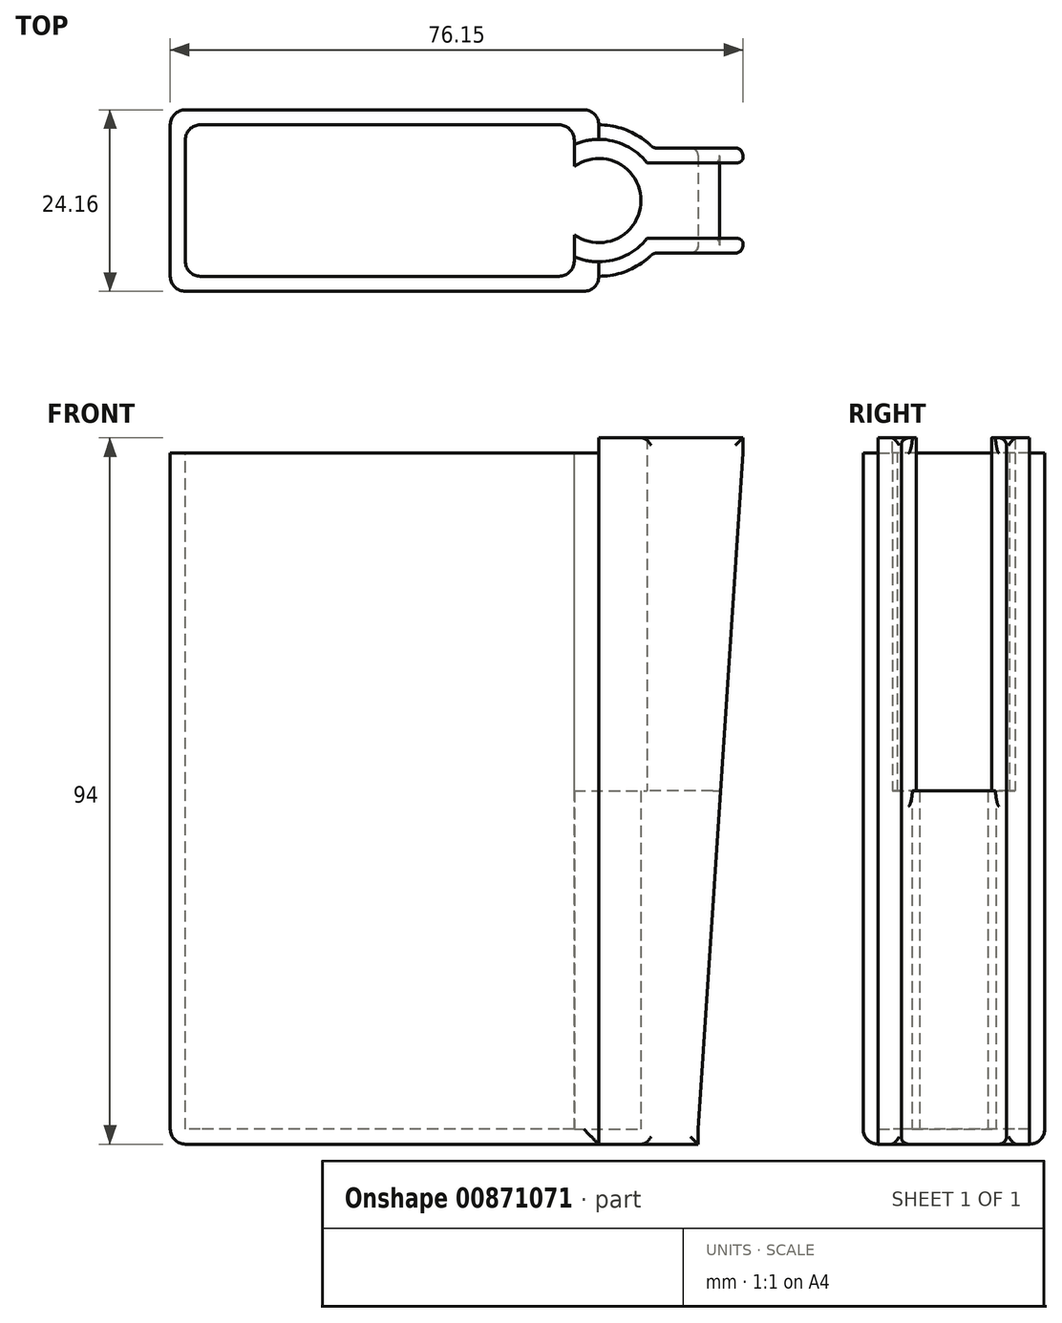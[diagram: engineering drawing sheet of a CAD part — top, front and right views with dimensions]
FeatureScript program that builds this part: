
annotation { "Feature Type Name" : "Feature", "Feature Type Description" : "" }
export const myFeature = defineFeature(function(context is Context, id is Id, definition is map)
    precondition{}
    {
        {
            var Q0;
            Q0=qCreatedBy(makeId("Top.planeOp"),FACE);
            var sketch = newSketch(context, id + "F0", { "sketchPlane" : qUnion([Q0])});
            skArc(sketch, "E0", {"start": v(6.44, 5) * mm, "mid": v(-8.15, 0) * mm, "end": v(6.44, -5) * mm});
            skLineSegment(sketch, "E1.bottom", {"start": v(19.15, 5) * mm, "end": v(8.66, 5) * mm});
            skLineSegment(sketch, "E1.top", {"start": v(19.15, -5) * mm, "end": v(8.66, -5) * mm});
            skLineSegment(sketch, "E2", {"start": v(-8.15, 0) * mm, "end": v(8.15, 0) * mm, "construction": true});
            skPoint(sketch, "E1.right.start.orphan", {"position": v(-27, 5) * mm});
            skPoint(sketch, "E3.orphan", {"position": v(-27, -5) * mm});
            skPoint(sketch, "E4.orphan", {"position": v(27, 5) * mm});
            skPoint(sketch, "E5.orphan", {"position": v(27, -5) * mm});
            skPoint(sketch, "E6.start.orphan", {"position": v(0, 8.15) * mm});
            skLineSegment(sketch, "E7.trimOffspring", {"start": v(10, 0) * mm, "end": v(19.15, 0) * mm, "construction": true});
            skArc(sketch, "E8", {"start": v(7.25, 7) * mm, "mid": v(-10.07, 0) * mm, "end": v(7.25, -7) * mm});
            skLineSegment(sketch, "E9", {"start": v(19.15, 7) * mm, "end": v(7.25, 7) * mm});
            skLineSegment(sketch, "E10", {"start": v(19.15, 7) * mm, "end": v(19.15, 5) * mm});
            skLineSegment(sketch, "E11.MirrorCS", {"start": v(19.15, -7) * mm, "end": v(7.25, -7) * mm});
            skLineSegment(sketch, "E12.MirrorCS", {"start": v(19.15, -7) * mm, "end": v(19.15, -5) * mm});
            skLineSegment(sketch, "E13", {"start": v(8.66, 5) * mm, "end": v(6.44, 5) * mm});
            skLineSegment(sketch, "E14.MirrorCS", {"start": v(8.66, -5) * mm, "end": v(6.44, -5) * mm});
            skLineSegment(sketch, "E15", {"start": v(19.15, -5) * mm, "end": v(19.15, 5) * mm});
            skSolve(sketch);
        }
        {
            var Q0;
            Q0=makeQuery(id+"F0.imprint","IMPRINT",FACE,{"disambiguationData":[TD([[makeQuery(id+"F0.imprint","IMPRINT",EDGE,{"derivedFrom":sQuery(id+"F0.wireOp",EDGE,"E0")}),-1.0]])]});
            extrude(context, id + "F1", {"entities" : qUnion([Q0]), "depth" : 90 * mm, "offsetDistance" : 25 * mm});
        }
        {
            var Q0;
            Q0 = qSketchRegion(id + "F0", true);
            extrude(context, id + "F2", {"entities" : qUnion([Q0]), "operationType" : NewBodyOperationType.ADD, "depth" : 43 * mm, "offsetDistance" : 25 * mm});
        }
        {
            var Q0;
            Q0=makeQuery(id+"F1.opExtrude","CAP_FACE",FACE,{"disambiguationData":[OSD([sQuery(id+"F0.wireOp",EDGE,"E0"),sQuery(id+"F0.wireOp",EDGE,"E1.bottom"),sQuery(id+"F0.wireOp",EDGE,"E1.top"),sQuery(id+"F0.wireOp",EDGE,"E8"),sQuery(id+"F0.wireOp",EDGE,"E9"),sQuery(id+"F0.wireOp",EDGE,"E10"),sQuery(id+"F0.wireOp",EDGE,"E11.MirrorCS"),sQuery(id+"F0.wireOp",EDGE,"E12.MirrorCS"),sQuery(id+"F0.wireOp",EDGE,"E13"),sQuery(id+"F0.wireOp",EDGE,"E14.MirrorCS")])],"isStart":false});
            var sketch = newSketch(context, id + "F3", { "sketchPlane" : qUnion([Q0])});
            skLineSegment(sketch, "E16", {"start": v(-3.27, -10.07) * mm, "end": v(-55, -10.07) * mm});
            skLineSegment(sketch, "E17.MirrorCS", {"start": v(-3.27, 10.07) * mm, "end": v(-55, 10.07) * mm});
            skLineSegment(sketch, "E18", {"start": v(-55, 10.07) * mm, "end": v(-55, -10.07) * mm});
            skPoint(sketch, "E19.start.orphan", {"position": v(0, 10.07) * mm});
            skLineSegment(sketch, "E20", {"start": v(0, 10.07) * mm, "end": v(0, 12.08) * mm});
            skLineSegment(sketch, "E21", {"start": v(0, 12.08) * mm, "end": v(-55, 12.08) * mm});
            skLineSegment(sketch, "E22", {"start": v(-55, 12.08) * mm, "end": v(-57, 12.08) * mm});
            skLineSegment(sketch, "E23.MirrorCS", {"start": v(0, -12.08) * mm, "end": v(-55, -12.08) * mm});
            skLineSegment(sketch, "E24.MirrorCS", {"start": v(-55, -12.08) * mm, "end": v(-57, -12.08) * mm});
            skLineSegment(sketch, "E25.MirrorCS", {"start": v(0, -10.07) * mm, "end": v(0, -12.08) * mm});
            skLineSegment(sketch, "E26", {"start": v(-57, 12.08) * mm, "end": v(-57, -12.08) * mm});
            skLineSegment(sketch, "E27", {"start": v(-3.27, 10.07) * mm, "end": v(-3.27, 9.53) * mm});
            skLineSegment(sketch, "E28", {"start": v(-3.27, 9.53) * mm, "end": v(-3.27, -10.07) * mm});
            skLineSegment(sketch, "E29", {"start": v(-10.07, 0) * mm, "end": v(-10.07, 10.08) * mm});
            skLineSegment(sketch, "E30", {"start": v(-10.07, 0) * mm, "end": v(-10.07, -10.07) * mm});
            skLineSegment(sketch, "E31.top", {"start": v(0, 8.22) * mm, "end": v(-3.27, 8.22) * mm});
            skLineSegment(sketch, "E31.left", {"start": v(0, 10.07) * mm, "end": v(0, 8.22) * mm});
            skLineSegment(sketch, "E31.right", {"start": v(-3.27, 10.07) * mm, "end": v(-3.27, 8.22) * mm});
            skLineSegment(sketch, "E32.MirrorCS", {"start": v(0, -8.22) * mm, "end": v(-3.27, -8.22) * mm});
            skLineSegment(sketch, "E33.MirrorCS", {"start": v(0, -10.07) * mm, "end": v(0, -8.22) * mm});
            skPoint(sketch, "E34.orphan", {"position": v(0, -10.07) * mm});
            skSolve(sketch);
        }
        {
            var Q0;
            {var subQ1=sQuery(id+"F3.wireOp",EDGE,"E18");Q0=makeQuery(id+"F3.imprint","IMPRINT",FACE,{"disambiguationData":[TD([[makeQuery(id+"F3.imprint","IMPRINT",EDGE,{"derivedFrom":subQ1}),-1.0]])]});}
            extrude(context, id + "F4", {"entities" : qUnion([Q0]), "oppositeDirection" : true, "depth" : 90 * mm, "offsetDistance" : 25 * mm});
        }
        {
            var Q0;
            {var subQ0=sQuery(id+"F3.wireOp",EDGE,"E28");var subQ4=makeQuery(id+"F1.opExtrude","CAP_EDGE",EDGE,{"disambiguationData":[OSD([sQuery(id+"F0.wireOp",EDGE,"E0")])],"isStart":false});var subQ6=makeQuery(id+"F3.imprint","INTERSECT",VERTEX,{"disambiguationData":[OD(1.0)],"derivedFrom":[subQ4,subQ0]});Q0=makeQuery(id+"F3.imprint","IMPRINT",FACE,{"disambiguationData":[TD([[makeQuery(id+"F3.imprint","IMPRINT",EDGE,{"disambiguationData":[TD([[subQ6,-1.0]])],"derivedFrom":subQ0}),-1.0]])]});}
            extrude(context, id + "F5", {"entities" : qUnion([Q0]), "operationType" : NewBodyOperationType.REMOVE, "oppositeDirection" : true, "depth" : 90 * mm, "offsetDistance" : 25 * mm});
        }
        {
            var Q0;
            {var subQ0=sQuery(id+"F3.wireOp",EDGE,"E28");var subQ1=makeQuery(id+"F1.opExtrude","CAP_EDGE",EDGE,{"disambiguationData":[OSD([sQuery(id+"F0.wireOp",EDGE,"E0")])],"isStart":false});var subQ2=makeQuery(id+"F3.imprint","INTERSECT",VERTEX,{"disambiguationData":[OD(0.0)],"derivedFrom":[subQ1,subQ0]});Q0=makeQuery(id+"F3.imprint","IMPRINT",FACE,{"disambiguationData":[TD([[makeQuery(id+"F3.imprint","IMPRINT",EDGE,{"disambiguationData":[TD([[subQ2,-1.0]])],"derivedFrom":subQ0}),-1.0]])]});}
            extrude(context, id + "F6", {"entities" : qUnion([Q0]), "operationType" : NewBodyOperationType.REMOVE, "oppositeDirection" : true, "depth" : 90 * mm, "offsetDistance" : 25 * mm});
        }
        {
            var Q0;
            Q0=makeQuery(id+"F2.opExtrude","CAP_FACE",FACE,{"disambiguationData":[OSD([sQuery(id+"F0.wireOp",EDGE,"E8"),sQuery(id+"F0.wireOp",EDGE,"E9"),sQuery(id+"F0.wireOp",EDGE,"E10"),sQuery(id+"F0.wireOp",EDGE,"E11.MirrorCS"),sQuery(id+"F0.wireOp",EDGE,"E12.MirrorCS"),sQuery(id+"F0.wireOp",EDGE,"E15")])],"isStart":false});
            var sketch = newSketch(context, id + "F7", { "sketchPlane" : qUnion([Q0])});
            skCircle(sketch, "E35", {"center": v(0, 0) * mm, "radius": 5.6 * mm});
            skSolve(sketch);
        }
        {
            var Q0;
            {var subQ0=sQuery(id+"F7.wireOp",EDGE,"E35");var subQ1=makeQuery(id+"F6.boolean.opBoolean","INTERSECT",EDGE,{"derivedFrom":[makeQuery(id+"F2.opExtrude","CAP_FACE",FACE,{"disambiguationData":[OSD([sQuery(id+"F0.wireOp",EDGE,"E8"),sQuery(id+"F0.wireOp",EDGE,"E9"),sQuery(id+"F0.wireOp",EDGE,"E10"),sQuery(id+"F0.wireOp",EDGE,"E11.MirrorCS"),sQuery(id+"F0.wireOp",EDGE,"E12.MirrorCS"),sQuery(id+"F0.wireOp",EDGE,"E15")])],"isStart":false}),makeQuery(id+"F6.opExtrude","SWEPT_FACE",FACE,{"disambiguationData":[OSD([sQuery(id+"F3.wireOp",EDGE,"E28")])]})]});var subQ2=makeQuery(id+"F7.imprint","INTERSECT",VERTEX,{"disambiguationData":[OD(0.0)],"derivedFrom":[subQ1,subQ0]});Q0=makeQuery(id+"F7.imprint","IMPRINT",FACE,{"disambiguationData":[TD([[makeQuery(id+"F7.imprint","IMPRINT",EDGE,{"disambiguationData":[TD([[subQ2,1.0]])],"derivedFrom":subQ0}),1.0]])]});}
            extrude(context, id + "F8", {"entities" : qUnion([Q0]), "operationType" : NewBodyOperationType.REMOVE, "oppositeDirection" : true, "depth" : 90 * mm, "offsetDistance" : 25 * mm});
        }
        {
            var Q0;
            Q0=makeQuery(id+"F1.opExtrude","SWEPT_FACE",FACE,{"disambiguationData":[OSD([sQuery(id+"F0.wireOp",EDGE,"E11.MirrorCS")])]});
            var sketch = newSketch(context, id + "F9", { "sketchPlane" : qUnion([Q0])});
            skLineSegment(sketch, "E36", {"start": v(19.15, 90) * mm, "end": v(13.2, 0) * mm});
            skSolve(sketch);
        }
        {
            var Q0;
            {var subQ0=sQuery(id+"F9.wireOp",EDGE,"E36");Q0=makeQuery(id+"F9.imprint","IMPRINT",FACE,{"disambiguationData":[TD([[makeQuery(id+"F9.imprint","IMPRINT",EDGE,{"derivedFrom":subQ0}),1.0]])]});}
            extrude(context, id + "F10", {"entities" : qUnion([Q0]), "operationType" : NewBodyOperationType.REMOVE, "oppositeDirection" : true, "depth" : 25 * mm, "offsetDistance" : 25 * mm});
        }
        {
            var Q0;
            Q0=makeQuery(id+"F2.opExtrude","CAP_FACE",FACE,{"disambiguationData":[OSD([sQuery(id+"F0.wireOp",EDGE,"E8"),sQuery(id+"F0.wireOp",EDGE,"E9"),sQuery(id+"F0.wireOp",EDGE,"E10"),sQuery(id+"F0.wireOp",EDGE,"E11.MirrorCS"),sQuery(id+"F0.wireOp",EDGE,"E12.MirrorCS"),sQuery(id+"F0.wireOp",EDGE,"E15")])],"isStart":false});
            extrude(context, id + "F11", {"entities" : qUnion([Q0]), "depth" : 2 * mm, "offsetDistance" : 25 * mm});
        }
        {
            var Q0;
            Q0=makeQuery(id+"F4.opExtrude","CAP_FACE",FACE,{"disambiguationData":[OSD([sQuery(id+"F3.wireOp",EDGE,"E16"),sQuery(id+"F3.wireOp",EDGE,"E17.MirrorCS"),sQuery(id+"F3.wireOp",EDGE,"E18"),sQuery(id+"F3.wireOp",EDGE,"E20"),sQuery(id+"F3.wireOp",EDGE,"E21"),sQuery(id+"F3.wireOp",EDGE,"E22"),sQuery(id+"F3.wireOp",EDGE,"E23.MirrorCS"),sQuery(id+"F3.wireOp",EDGE,"E24.MirrorCS"),sQuery(id+"F3.wireOp",EDGE,"E25.MirrorCS"),sQuery(id+"F3.wireOp",EDGE,"E26")])],"isStart":false});
            var sketch = newSketch(context, id + "F12", { "sketchPlane" : qUnion([Q0])});
            skLineSegment(sketch, "E37.bottom", {"start": v(-57, 12.08) * mm, "end": v(0, 12.08) * mm});
            skLineSegment(sketch, "E37.top", {"start": v(-57, -12.08) * mm, "end": v(0, -12.08) * mm});
            skLineSegment(sketch, "E37.left", {"start": v(-57, 12.08) * mm, "end": v(-57, -12.08) * mm});
            skLineSegment(sketch, "E37.right", {"start": v(0, 12.08) * mm, "end": v(0, -12.08) * mm});
            skCircle(sketch, "E38", {"center": v(0, 0) * mm, "radius": 10.07 * mm});
            skSolve(sketch);
        }
        {
            var Q0;
            {var subQ0=sQuery(id+"F3.wireOp",EDGE,"E32.MirrorCS");Q0=makeQuery(id+"F3.imprint","IMPRINT",FACE,{"disambiguationData":[TD([[makeQuery(id+"F3.imprint","IMPRINT",EDGE,{"derivedFrom":subQ0}),1.0]])]});}
            var Q1;
            {var subQ0=sQuery(id+"F3.wireOp",EDGE,"E31.top");Q1=makeQuery(id+"F3.imprint","IMPRINT",FACE,{"disambiguationData":[TD([[makeQuery(id+"F3.imprint","IMPRINT",EDGE,{"derivedFrom":subQ0}),-1.0]])]});}
            extrude(context, id + "F13", {"entities" : qUnion([Q0, Q1]), "oppositeDirection" : true, "depth" : 90 * mm, "offsetDistance" : 25 * mm});
        }
        {
            var Q0;
            Q0=makeQuery(id+"F4.opExtrude","SWEPT_BODY",BODY,{"disambiguationData":[OSD([sQuery(id+"F0.wireOp",EDGE,"E8"),sQuery(id+"F3.wireOp",EDGE,"E16"),sQuery(id+"F3.wireOp",EDGE,"E17.MirrorCS"),sQuery(id+"F3.wireOp",EDGE,"E18"),sQuery(id+"F3.wireOp",EDGE,"E20"),sQuery(id+"F3.wireOp",EDGE,"E21"),sQuery(id+"F3.wireOp",EDGE,"E22"),sQuery(id+"F3.wireOp",EDGE,"E23.MirrorCS"),sQuery(id+"F3.wireOp",EDGE,"E24.MirrorCS"),sQuery(id+"F3.wireOp",EDGE,"E25.MirrorCS"),sQuery(id+"F3.wireOp",EDGE,"E26"),sQuery(id+"F3.wireOp",EDGE,"E28"),sQuery(id+"F3.wireOp",EDGE,"E31.right")])]});
            var Q1;
            Q1=makeQuery(id+"F11.opExtrude","SWEPT_BODY",BODY,{"disambiguationData":[OSD([sQuery(id+"F0.wireOp",EDGE,"E8"),sQuery(id+"F0.wireOp",EDGE,"E9"),sQuery(id+"F0.wireOp",EDGE,"E10"),sQuery(id+"F0.wireOp",EDGE,"E11.MirrorCS"),sQuery(id+"F0.wireOp",EDGE,"E12.MirrorCS"),sQuery(id+"F0.wireOp",EDGE,"E15")])]});
            var Q2;
            Q2=makeQuery(id+"F1.opExtrude","SWEPT_BODY",BODY,{"disambiguationData":[OSD([sQuery(id+"F0.wireOp",EDGE,"E0"),sQuery(id+"F0.wireOp",EDGE,"E1.bottom"),sQuery(id+"F0.wireOp",EDGE,"E1.top"),sQuery(id+"F0.wireOp",EDGE,"E8"),sQuery(id+"F0.wireOp",EDGE,"E9"),sQuery(id+"F0.wireOp",EDGE,"E10"),sQuery(id+"F0.wireOp",EDGE,"E11.MirrorCS"),sQuery(id+"F0.wireOp",EDGE,"E12.MirrorCS"),sQuery(id+"F0.wireOp",EDGE,"E13"),sQuery(id+"F0.wireOp",EDGE,"E14.MirrorCS")])]});
            var Q3;
            Q3=makeQuery(id+"F13.opExtrude","SWEPT_BODY",BODY,{"disambiguationData":[OSD([sQuery(id+"F0.wireOp",EDGE,"E8"),sQuery(id+"F3.wireOp",EDGE,"E28"),sQuery(id+"F3.wireOp",EDGE,"E32.MirrorCS"),sQuery(id+"F3.wireOp",EDGE,"E33.MirrorCS")])]});
            var Q4;
            Q4=makeQuery(id+"F13.opExtrude","SWEPT_BODY",BODY,{"disambiguationData":[OSD([sQuery(id+"F0.wireOp",EDGE,"E8"),sQuery(id+"F3.wireOp",EDGE,"E31.top"),sQuery(id+"F3.wireOp",EDGE,"E31.left"),sQuery(id+"F3.wireOp",EDGE,"E31.right")])]});
            booleanBodies(context, id + "F14", {"operationType" : BooleanOperationType.UNION, "tools" : qUnion([Q0, Q1, Q2, Q3, Q4])});
        }
        {
            var Q0;
            {var subQ0=sQuery(id+"F0.wireOp",EDGE,"E12.MirrorCS");var subQ1=sQuery(id+"F0.wireOp",EDGE,"E11.MirrorCS");var subQ2=sQuery(id+"F0.wireOp",EDGE,"E10");var subQ3=sQuery(id+"F0.wireOp",EDGE,"E9");var subQ4=sQuery(id+"F0.wireOp",EDGE,"E8");Q0=makeQuery(id+"F14.opBoolean","MERGE",FACE,{"derivedFrom":[makeQuery(id+"F4.opExtrude","CAP_FACE",FACE,{"disambiguationData":[OSD([subQ4,sQuery(id+"F3.wireOp",EDGE,"E16"),sQuery(id+"F3.wireOp",EDGE,"E17.MirrorCS"),sQuery(id+"F3.wireOp",EDGE,"E18"),sQuery(id+"F3.wireOp",EDGE,"E20"),sQuery(id+"F3.wireOp",EDGE,"E21"),sQuery(id+"F3.wireOp",EDGE,"E22"),sQuery(id+"F3.wireOp",EDGE,"E23.MirrorCS"),sQuery(id+"F3.wireOp",EDGE,"E24.MirrorCS"),sQuery(id+"F3.wireOp",EDGE,"E25.MirrorCS"),sQuery(id+"F3.wireOp",EDGE,"E26"),sQuery(id+"F3.wireOp",EDGE,"E28"),sQuery(id+"F3.wireOp",EDGE,"E31.right")])],"isStart":false}),makeQuery(id+"F2.boolean.opBoolean","MERGE",FACE,{"derivedFrom":[makeQuery(id+"F1.opExtrude","CAP_FACE",FACE,{"disambiguationData":[OSD([sQuery(id+"F0.wireOp",EDGE,"E0"),sQuery(id+"F0.wireOp",EDGE,"E1.bottom"),sQuery(id+"F0.wireOp",EDGE,"E1.top"),subQ4,subQ3,subQ2,subQ1,subQ0,sQuery(id+"F0.wireOp",EDGE,"E13"),sQuery(id+"F0.wireOp",EDGE,"E14.MirrorCS")])],"isStart":true}),makeQuery(id+"F2.opExtrude","CAP_FACE",FACE,{"disambiguationData":[OSD([subQ4,subQ3,subQ2,subQ1,subQ0,sQuery(id+"F0.wireOp",EDGE,"E15")])],"isStart":true})]})]});}
            var Q1;
            Q1=makeQuery(id+"F12.imprint","IMPRINT",FACE,{"disambiguationData":[TD([[makeQuery(id+"F12.imprint","IMPRINT",EDGE,{"derivedFrom":makeQuery(id+"F4.opExtrude","CAP_EDGE",EDGE,{"disambiguationData":[OSD([sQuery(id+"F3.wireOp",EDGE,"E16")])],"isStart":false})}),1.0]])]});
            var Q2;
            {var subQ0=sQuery(id+"F12.wireOp",EDGE,"E38");var subQ1=sQuery(id+"F12.wireOp",EDGE,"E37.right");var subQ2=makeQuery(id+"F12.imprint","INTERSECT",VERTEX,{"disambiguationData":[OD(0.0)],"derivedFrom":[subQ1,subQ0]});Q2=makeQuery(id+"F12.imprint","IMPRINT",FACE,{"disambiguationData":[TD([[makeQuery(id+"F12.imprint","IMPRINT",EDGE,{"disambiguationData":[TD([[subQ2,1.0]])],"derivedFrom":subQ1}),-1.0]])]});}
            var Q3;
            {var subQ0=sQuery(id+"F12.wireOp",EDGE,"E38");var subQ1=sQuery(id+"F12.wireOp",EDGE,"E37.right");var subQ2=makeQuery(id+"F12.imprint","INTERSECT",VERTEX,{"disambiguationData":[OD(0.0)],"derivedFrom":[subQ1,subQ0]});Q3=makeQuery(id+"F12.imprint","IMPRINT",FACE,{"disambiguationData":[TD([[makeQuery(id+"F12.imprint","IMPRINT",EDGE,{"disambiguationData":[TD([[subQ2,1.0]])],"derivedFrom":subQ1}),1.0]])]});}
            extrude(context, id + "F15", {"entities" : qUnion([Q0, Q1, Q2, Q3]), "operationType" : NewBodyOperationType.ADD, "depth" : 2 * mm, "offsetDistance" : 25 * mm});
        }
        {
            var Q0;
            {var subQ5=sQuery(id+"F3.wireOp",EDGE,"E31.top");Q0=makeQuery(id+"F3.imprint","IMPRINT",FACE,{"disambiguationData":[TD([[makeQuery(id+"F3.imprint","IMPRINT",EDGE,{"derivedFrom":subQ5}),1.0]])]});}
            var Q1;
            {var subQ1=sQuery(id+"F3.wireOp",EDGE,"E32.MirrorCS");Q1=makeQuery(id+"F3.imprint","IMPRINT",FACE,{"disambiguationData":[TD([[makeQuery(id+"F3.imprint","IMPRINT",EDGE,{"derivedFrom":subQ1}),-1.0]])]});}
            extrude(context, id + "F16", {"entities" : qUnion([Q0, Q1]), "operationType" : NewBodyOperationType.ADD, "depth" : 2 * mm, "offsetDistance" : 25 * mm});
        }
        {
            var Q0;
            Q0=makeQuery(id+"F16.opExtrude","CAP_FACE",FACE,{"disambiguationData":[OSD([sQuery(id+"F0.wireOp",EDGE,"E0"),sQuery(id+"F0.wireOp",EDGE,"E1.top"),sQuery(id+"F0.wireOp",EDGE,"E8"),sQuery(id+"F0.wireOp",EDGE,"E11.MirrorCS"),sQuery(id+"F0.wireOp",EDGE,"E12.MirrorCS"),sQuery(id+"F0.wireOp",EDGE,"E14.MirrorCS"),sQuery(id+"F3.wireOp",EDGE,"E28"),sQuery(id+"F3.wireOp",EDGE,"E32.MirrorCS"),sQuery(id+"F3.wireOp",EDGE,"E33.MirrorCS")])],"isStart":false});
            var sketch = newSketch(context, id + "F17", { "sketchPlane" : qUnion([Q0])});
            skLineSegment(sketch, "E39.bottom", {"start": v(0, -10.07) * mm, "end": v(-6.2, -10.07) * mm});
            skLineSegment(sketch, "E39.top", {"start": v(0, 10.1) * mm, "end": v(-6.2, 10.1) * mm});
            skLineSegment(sketch, "E39.left", {"start": v(0, -10.08) * mm, "end": v(0, 10.1) * mm});
            skLineSegment(sketch, "E39.right", {"start": v(-6.2, -10.08) * mm, "end": v(-6.2, 10.1) * mm});
            skSolve(sketch);
        }
        {
            var Q0;
            {var subQ1=sQuery(id+"F17.wireOp",EDGE,"E39.bottom");Q0=makeQuery(id+"F17.imprint","IMPRINT",FACE,{"disambiguationData":[TD([[makeQuery(id+"F17.imprint","IMPRINT",EDGE,{"derivedFrom":subQ1}),-1.0]])]});}
            extrude(context, id + "F18", {"entities" : qUnion([Q0]), "operationType" : NewBodyOperationType.REMOVE, "oppositeDirection" : true, "depth" : 2 * mm, "offsetDistance" : 25 * mm});
        }
        {
            var Q0;
            Q0=makeQuery(id+"F16.opExtrude","CAP_FACE",FACE,{"disambiguationData":[OSD([sQuery(id+"F0.wireOp",EDGE,"E0"),sQuery(id+"F0.wireOp",EDGE,"E1.top"),sQuery(id+"F0.wireOp",EDGE,"E8"),sQuery(id+"F0.wireOp",EDGE,"E11.MirrorCS"),sQuery(id+"F0.wireOp",EDGE,"E12.MirrorCS"),sQuery(id+"F0.wireOp",EDGE,"E14.MirrorCS"),sQuery(id+"F3.wireOp",EDGE,"E28"),sQuery(id+"F3.wireOp",EDGE,"E32.MirrorCS"),sQuery(id+"F3.wireOp",EDGE,"E33.MirrorCS")])],"isStart":false});
            var sketch = newSketch(context, id + "F19", { "sketchPlane" : qUnion([Q0])});
            skLineSegment(sketch, "E40.bottom", {"start": v(0, -10.07) * mm, "end": v(-3.96, -10.07) * mm});
            skLineSegment(sketch, "E40.top", {"start": v(0, -6.7) * mm, "end": v(-3.96, -6.7) * mm});
            skLineSegment(sketch, "E40.left", {"start": v(0, -10.07) * mm, "end": v(0, -6.7) * mm});
            skLineSegment(sketch, "E40.right", {"start": v(-3.96, -10.07) * mm, "end": v(-3.96, -6.7) * mm});
            skSolve(sketch);
        }
        {
            var Q0;
            {var subQ1=sQuery(id+"F3.wireOp",EDGE,"E32.MirrorCS");var subQ2=makeQuery(id+"F16.opExtrude","CAP_EDGE",EDGE,{"disambiguationData":[OSD([subQ1])],"isStart":false});Q0=makeQuery(id+"F19.imprint","IMPRINT",FACE,{"disambiguationData":[TD([[makeQuery(id+"F19.imprint","IMPRINT",EDGE,{"derivedFrom":subQ2}),-1.0]])]});}
            extrude(context, id + "F20", {"entities" : qUnion([Q0]), "operationType" : NewBodyOperationType.REMOVE, "oppositeDirection" : true, "depth" : 2 * mm, "offsetDistance" : 25 * mm});
        }
        {
            var Q0;
            {var subQ0=sQuery(id+"F0.wireOp",EDGE,"E9");Q0=makeQuery(id+"F16.boolean.opBoolean","MERGE",FACE,{"derivedFrom":[makeQuery(id+"F15.boolean.opBoolean","MERGE",FACE,{"derivedFrom":[makeQuery(id+"F1.opExtrude","SWEPT_FACE",FACE,{"disambiguationData":[OSD([subQ0])]}),makeQuery(id+"F15.opExtrude","SWEPT_FACE",FACE,{"disambiguationData":[OSD([subQ0])]})]}),makeQuery(id+"F16.opExtrude","SWEPT_FACE",FACE,{"disambiguationData":[OSD([subQ0])]})]});}
            var Q1;
            {var subQ0=sQuery(id+"F0.wireOp",EDGE,"E11.MirrorCS");Q1=makeQuery(id+"F16.boolean.opBoolean","MERGE",FACE,{"derivedFrom":[makeQuery(id+"F15.boolean.opBoolean","MERGE",FACE,{"derivedFrom":[makeQuery(id+"F1.opExtrude","SWEPT_FACE",FACE,{"disambiguationData":[OSD([subQ0])]}),makeQuery(id+"F15.opExtrude","SWEPT_FACE",FACE,{"disambiguationData":[OSD([subQ0])]})]}),makeQuery(id+"F16.opExtrude","SWEPT_FACE",FACE,{"disambiguationData":[OSD([subQ0])]})]});}
            var Q2;
            Q2=makeQuery(id+"F10.boolean.opBoolean","COPY",FACE,{"derivedFrom":makeQuery(id+"F10.opExtrude","SWEPT_FACE",FACE,{"disambiguationData":[OSD([sQuery(id+"F9.wireOp",EDGE,"E36")])]})});
            fillet(context, id + "F21", {"entities" : qUnion([Q0, Q1, Q2]), "radius" : 1 * mm, "tangentPropagation" : true, "allowEdgeOverflow" : false});
        }
        {
            var Q0;
            {var subQ0=sQuery(id+"F3.wireOp",EDGE,"E26");var subQ1=sQuery(id+"F3.wireOp",EDGE,"E24.MirrorCS");Q0=makeQuery(id+"F15.boolean.opBoolean","MERGE",EDGE,{"derivedFrom":[makeQuery(id+"F4.opExtrude","SWEPT_EDGE",EDGE,{"disambiguationData":[OSD([subQ1,subQ0])]}),makeQuery(id+"F15.opExtrude","SWEPT_EDGE",EDGE,{"disambiguationData":[OSD([subQ1,subQ0])]})]});}
            var Q1;
            Q1=makeQuery(id+"F4.opExtrude","SWEPT_EDGE",EDGE,{"disambiguationData":[OSD([sQuery(id+"F3.wireOp",EDGE,"E17.MirrorCS"),sQuery(id+"F3.wireOp",EDGE,"E31.right")])]});
            var Q2;
            Q2=makeQuery(id+"F4.opExtrude","SWEPT_EDGE",EDGE,{"disambiguationData":[OSD([sQuery(id+"F3.wireOp",EDGE,"E16"),sQuery(id+"F3.wireOp",EDGE,"E28")])]});
            var Q3;
            Q3=makeQuery(id+"F4.opExtrude","SWEPT_EDGE",EDGE,{"disambiguationData":[OSD([sQuery(id+"F3.wireOp",EDGE,"E17.MirrorCS"),sQuery(id+"F3.wireOp",EDGE,"E18")])]});
            var Q4;
            Q4=makeQuery(id+"F4.opExtrude","CAP_EDGE",EDGE,{"disambiguationData":[OSD([sQuery(id+"F3.wireOp",EDGE,"E17.MirrorCS")])],"isStart":false});
            var Q5;
            Q5=makeQuery(id+"F4.opExtrude","CAP_EDGE",EDGE,{"disambiguationData":[OSD([sQuery(id+"F3.wireOp",EDGE,"E16")])],"isStart":false});
            var Q6;
            Q6=makeQuery(id+"F4.opExtrude","CAP_EDGE",EDGE,{"disambiguationData":[OSD([sQuery(id+"F3.wireOp",EDGE,"E18")])],"isStart":false});
            var Q7;
            Q7=makeQuery(id+"F4.opExtrude","SWEPT_EDGE",EDGE,{"disambiguationData":[OSD([sQuery(id+"F3.wireOp",EDGE,"E16"),sQuery(id+"F3.wireOp",EDGE,"E18")])]});
            var Q8;
            {var subQ0=sQuery(id+"F3.wireOp",EDGE,"E28");var subQ1=sQuery(id+"F3.wireOp",EDGE,"E31.right");Q8=makeQuery(id+"F14.opBoolean","MERGE",EDGE,{"derivedFrom":[makeQuery(id+"F4.opExtrude","CAP_EDGE",EDGE,{"disambiguationData":[OSD([subQ1])],"isStart":false}),makeQuery(id+"F8.boolean.opBoolean","SPLIT",EDGE,{"disambiguationData":[OD(0.0)],"derivedFrom":makeQuery(id+"F6.boolean.opBoolean","MERGE",EDGE,{"derivedFrom":[makeQuery(id+"F5.boolean.opBoolean","COPY",EDGE,{"derivedFrom":makeQuery(id+"F5.opExtrude","CAP_EDGE",EDGE,{"disambiguationData":[OSD([subQ0,subQ1])],"isStart":false})}),makeQuery(id+"F5.boolean.opBoolean","COPY",EDGE,{"derivedFrom":makeQuery(id+"F5.opExtrude","CAP_EDGE",EDGE,{"disambiguationData":[OSD([subQ0])],"isStart":false})}),makeQuery(id+"F6.opExtrude","CAP_EDGE",EDGE,{"disambiguationData":[OSD([subQ0])],"isStart":false})]})})]});}
            var Q9;
            {var subQ0=sQuery(id+"F3.wireOp",EDGE,"E28");Q9=makeQuery(id+"F14.opBoolean","MERGE",EDGE,{"derivedFrom":[makeQuery(id+"F4.opExtrude","CAP_EDGE",EDGE,{"disambiguationData":[OSD([subQ0])],"isStart":false}),makeQuery(id+"F8.boolean.opBoolean","SPLIT",EDGE,{"disambiguationData":[OD(1.0)],"derivedFrom":makeQuery(id+"F6.boolean.opBoolean","MERGE",EDGE,{"derivedFrom":[makeQuery(id+"F5.boolean.opBoolean","COPY",EDGE,{"derivedFrom":makeQuery(id+"F5.opExtrude","CAP_EDGE",EDGE,{"disambiguationData":[OSD([subQ0,sQuery(id+"F3.wireOp",EDGE,"E31.right")])],"isStart":false})}),makeQuery(id+"F5.boolean.opBoolean","COPY",EDGE,{"derivedFrom":makeQuery(id+"F5.opExtrude","CAP_EDGE",EDGE,{"disambiguationData":[OSD([subQ0])],"isStart":false})}),makeQuery(id+"F6.opExtrude","CAP_EDGE",EDGE,{"disambiguationData":[OSD([subQ0])],"isStart":false})]})})]});}
            var Q10;
            {var subQ0=sQuery(id+"F3.wireOp",EDGE,"E26");var subQ1=sQuery(id+"F3.wireOp",EDGE,"E22");Q10=makeQuery(id+"F15.boolean.opBoolean","MERGE",EDGE,{"derivedFrom":[makeQuery(id+"F4.opExtrude","SWEPT_EDGE",EDGE,{"disambiguationData":[OSD([subQ1,subQ0])]}),makeQuery(id+"F15.opExtrude","SWEPT_EDGE",EDGE,{"disambiguationData":[OSD([subQ1,subQ0])]})]});}
            var Q11;
            {var subQ0=sQuery(id+"F3.wireOp",EDGE,"E25.MirrorCS");var subQ1=sQuery(id+"F3.wireOp",EDGE,"E23.MirrorCS");Q11=makeQuery(id+"F15.boolean.opBoolean","MERGE",EDGE,{"derivedFrom":[makeQuery(id+"F4.opExtrude","SWEPT_EDGE",EDGE,{"disambiguationData":[OSD([subQ1,subQ0])]}),makeQuery(id+"F15.opExtrude","SWEPT_EDGE",EDGE,{"disambiguationData":[OSD([subQ1,subQ0])]})]});}
            var Q12;
            {var subQ0=sQuery(id+"F3.wireOp",EDGE,"E21");var subQ1=sQuery(id+"F3.wireOp",EDGE,"E20");Q12=makeQuery(id+"F15.boolean.opBoolean","MERGE",EDGE,{"derivedFrom":[makeQuery(id+"F4.opExtrude","SWEPT_EDGE",EDGE,{"disambiguationData":[OSD([subQ1,subQ0])]}),makeQuery(id+"F15.opExtrude","SWEPT_EDGE",EDGE,{"disambiguationData":[OSD([subQ1,subQ0])]})]});}
            var Q13;
            Q13=makeQuery(id+"F15.opExtrude","CAP_EDGE",EDGE,{"disambiguationData":[OSD([sQuery(id+"F3.wireOp",EDGE,"E23.MirrorCS"),sQuery(id+"F3.wireOp",EDGE,"E24.MirrorCS")])],"isStart":false});
            var Q14;
            Q14=makeQuery(id+"F15.opExtrude","CAP_EDGE",EDGE,{"disambiguationData":[OSD([sQuery(id+"F3.wireOp",EDGE,"E21"),sQuery(id+"F3.wireOp",EDGE,"E22")])],"isStart":false});
            var Q15;
            Q15=makeQuery(id+"F15.opExtrude","CAP_EDGE",EDGE,{"disambiguationData":[OSD([sQuery(id+"F3.wireOp",EDGE,"E26")])],"isStart":false});
            var Q16;
            Q16=makeQuery(id+"F15.opExtrude","CAP_EDGE",EDGE,{"disambiguationData":[OSD([sQuery(id+"F0.wireOp",EDGE,"E11.MirrorCS"),sQuery(id+"F9.wireOp",EDGE,"E36")])],"isStart":false});
            fillet(context, id + "F22", {"entities" : qUnion([Q0, Q1, Q2, Q3, Q4, Q5, Q6, Q7, Q8, Q9, Q10, Q11, Q12, Q13, Q14, Q15, Q16]), "radius" : 2 * mm, "tangentPropagation" : true, "allowEdgeOverflow" : false});
        }
    });
